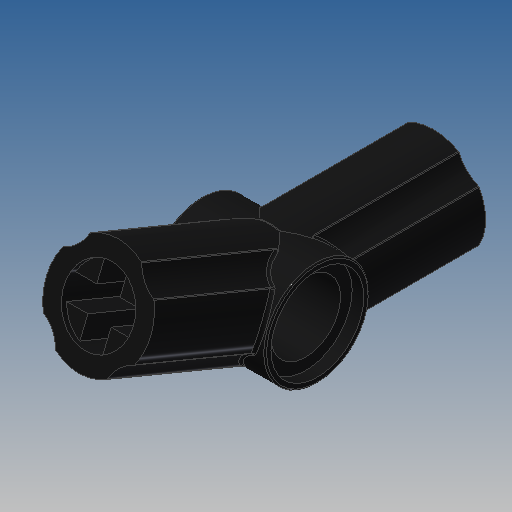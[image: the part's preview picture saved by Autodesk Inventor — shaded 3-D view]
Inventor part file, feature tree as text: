
AUTODESK INVENTOR PART (.ipt)
format: ipt  version: 2022.2 (Build 262287000, 287)  size: 550,400 bytes
history: native  units: mm (DEFAULTED — no unit token found)
features: extrude x5, sketch x5, pattern_circular x1, hole x1, fillet x1, other x1
bodies: Solid1 (feature_tree)
feature tree (14):
  extrude  "Extrusion1"  Depth=7.2mm
  sketch  "Sketch20"  dims[d49=7.2mm d50=4.8mm d51=1.6mm d55=0.2mm d56=0.1mm d57=20.0mm d58=157.5deg d60=4.8mm d61=8.0mm d62=0.0mm d63=1.6mm d64=0.4mm d65=0.0mm]
  extrude  "Extrusion15"  Depth=8.0mm TaperAngle=0.0deg
  extrude  "Extrusion16"  Depth=8.0mm
  pattern_circular  "Circular Pattern1"  [2 undecoded]
  extrude  "Extrusion4"  Depth=8.0mm
  hole  "Hole1"  [1 undecoded]
  extrude  "Extrusion9"  Depth=0.1mm TaperAngle=157.5deg
  fillet  "Fillet1"  Radius=4.8mm
  other  "Origin Point"
  sketch  "Skizze1"  dims[d1=0.0mm d8=7.2mm]
  sketch  "Sketch6"  dims[d9=8.0mm d10=0.0mm]
  sketch  "Sketch12"  dims[d24=4.8mm d25=6.0mm d26=6.4mm d27=0.8mm d28=90.0deg d29=8.0mm d30=0.0mm d32=0.8mm d33=0.0mm]
  sketch  "Sketch13"  dims[d46=8.0mm d47=7.5mm d48=2.4mm]
note: 3 required parameter values undecoded (feature->parameter linkage not recoverable at this tier; creation-order binding heuristic only, values carry confidence <= 0.55)
